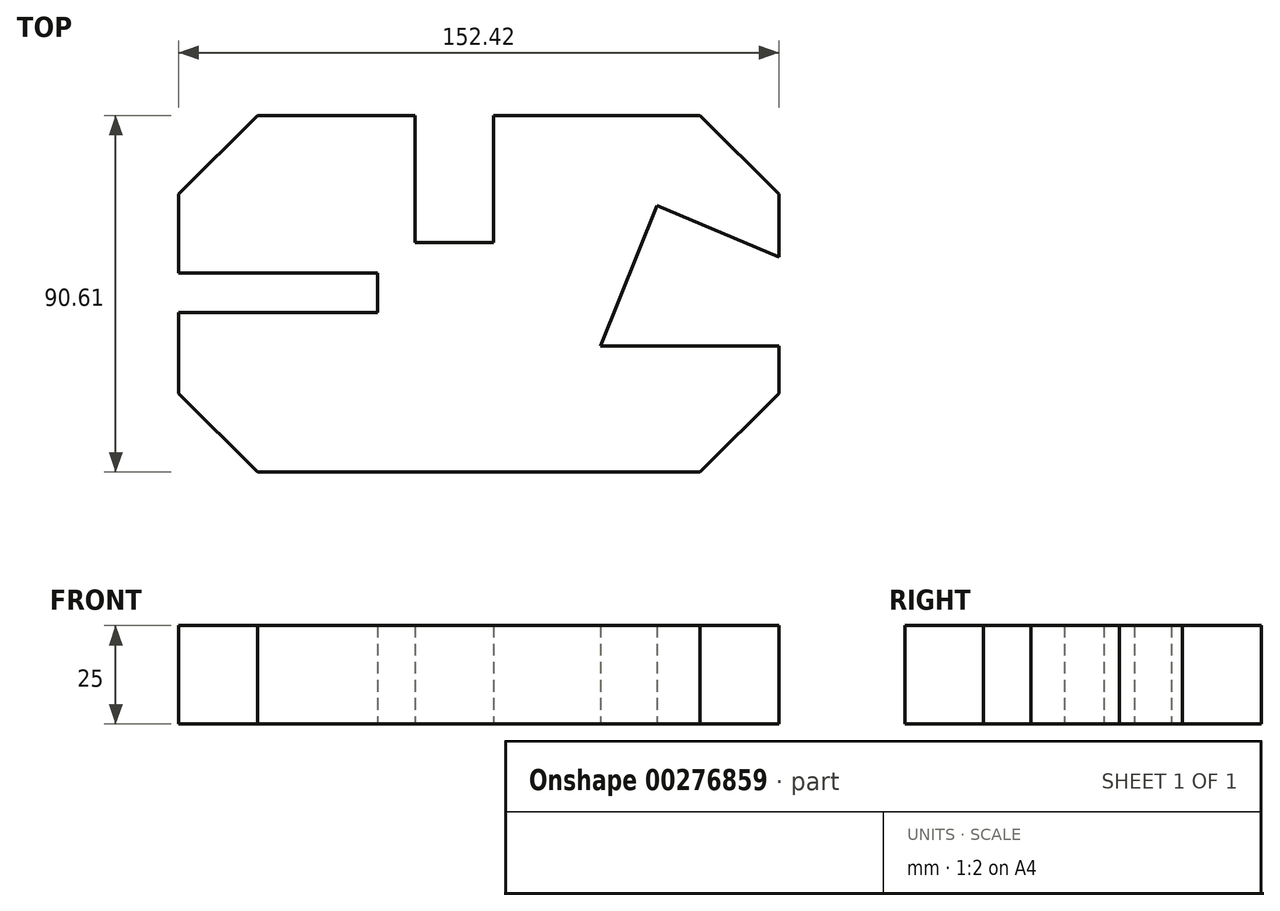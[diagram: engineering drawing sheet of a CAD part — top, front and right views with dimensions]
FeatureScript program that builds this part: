
annotation { "Feature Type Name" : "Feature", "Feature Type Description" : "" }
export const myFeature = defineFeature(function(context is Context, id is Id, definition is map)
    precondition{}
    {
        {
            var Q0;
            Q0=qCreatedBy(makeId("Top.planeOp"),FACE);
            var sketch = newSketch(context, id + "F0", { "sketchPlane" : qUnion([Q0])});
            skLineSegment(sketch, "E0", {"start": v(-37.27, -17.87) * mm, "end": v(75.13, -17.87) * mm});
            skLineSegment(sketch, "E1", {"start": v(75.13, -17.87) * mm, "end": v(95.14, 2.14) * mm});
            skLineSegment(sketch, "E2", {"start": v(95.14, 2.14) * mm, "end": v(95.14, 14.14) * mm});
            skLineSegment(sketch, "E3", {"start": v(95.14, 14.14) * mm, "end": v(49.84, 14.14) * mm});
            skLineSegment(sketch, "E4", {"start": v(49.84, 14.14) * mm, "end": v(64.26, 49.83) * mm});
            skLineSegment(sketch, "E5", {"start": v(64.26, 49.83) * mm, "end": v(95.14, 36.73) * mm});
            skLineSegment(sketch, "E6", {"start": v(95.14, 36.73) * mm, "end": v(95.14, 52.73) * mm});
            skLineSegment(sketch, "E7", {"start": v(95.14, 52.73) * mm, "end": v(75.13, 72.74) * mm});
            skLineSegment(sketch, "E8", {"start": v(75.13, 72.74) * mm, "end": v(22.73, 72.74) * mm});
            skLineSegment(sketch, "E9", {"start": v(22.73, 72.74) * mm, "end": v(22.73, 40.44) * mm});
            skLineSegment(sketch, "E10", {"start": v(22.73, 40.44) * mm, "end": v(2.73, 40.44) * mm});
            skLineSegment(sketch, "E11", {"start": v(2.73, 40.44) * mm, "end": v(2.73, 72.74) * mm});
            skLineSegment(sketch, "E12", {"start": v(2.73, 72.74) * mm, "end": v(-37.27, 72.74) * mm});
            skLineSegment(sketch, "E13", {"start": v(-37.27, 72.74) * mm, "end": v(-57.28, 52.73) * mm});
            skLineSegment(sketch, "E14", {"start": v(-57.28, 52.73) * mm, "end": v(-57.28, 32.73) * mm});
            skLineSegment(sketch, "E15", {"start": v(-57.28, 32.73) * mm, "end": v(-6.78, 32.73) * mm});
            skLineSegment(sketch, "E16", {"start": v(-6.78, 32.73) * mm, "end": v(-6.78, 22.73) * mm});
            skLineSegment(sketch, "E17", {"start": v(-6.78, 22.73) * mm, "end": v(-57.28, 22.73) * mm});
            skLineSegment(sketch, "E18", {"start": v(-57.28, 22.73) * mm, "end": v(-57.28, 2.14) * mm});
            skLineSegment(sketch, "E19", {"start": v(-57.28, 2.14) * mm, "end": v(-37.27, -17.87) * mm});
            skSolve(sketch);
        }
        {
            var Q0;
            Q0 = qSketchRegion(id + "F0", true);
            extrude(context, id + "F1", {"entities" : qUnion([Q0]), "depth" : 25 * mm});
        }
    });
